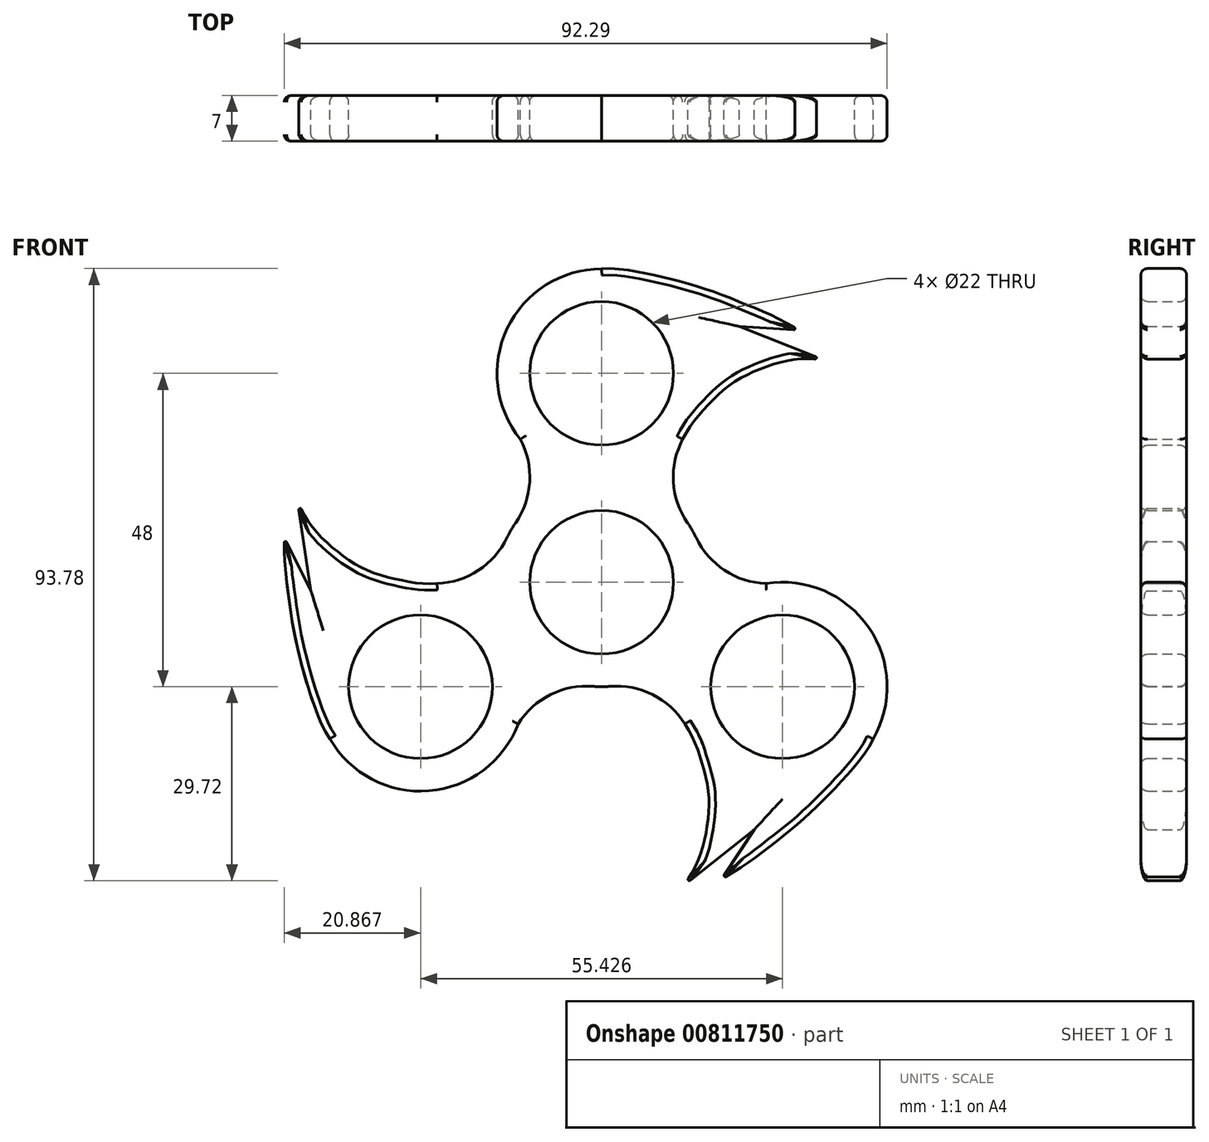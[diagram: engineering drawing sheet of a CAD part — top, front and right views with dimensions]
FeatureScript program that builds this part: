
annotation { "Feature Type Name" : "Feature", "Feature Type Description" : "" }
export const myFeature = defineFeature(function(context is Context, id is Id, definition is map)
    precondition{}
    {
        {
            var Q0;
            Q0=qCreatedBy(makeId("Front.planeOp"),FACE);
            var sketch = newSketch(context, id + "F0", { "sketchPlane" : qUnion([Q0])});
            skCircle(sketch, "E0", {"center": v(0, 0) * mm, "radius": 11 * mm});
            skArc(sketch, "E1", {"start": v(-13.17, 9.09) * mm, "mid": v(0, -16) * mm, "end": v(13.17, 9.09) * mm});
            skCircle(sketch, "E2", {"center": v(0, 32) * mm, "radius": 11 * mm});
            skLineSegment(sketch, "E3", {"start": v(12.42, 21.9) * mm, "end": v(12.42, 21.9) * mm});
            skFitSpline(sketch, "E4", {"points": [v(0, 48) * mm, v(15.63, 45) * mm, v(22.11, 42.54) * mm, v(30.28, 38.63) * mm], "startDerivative": vector(23.83, 2.95) * mm, "endDerivative": vector(45.32, -25.65) * mm});
            skLineSegment(sketch, "E5", {"start": v(30.28, 38.63) * mm, "end": v(21.1, 39.2) * mm});
            skLineSegment(sketch, "E6", {"start": v(21.1, 39.2) * mm, "end": v(34.96, 33.72) * mm});
            skFitSpline(sketch, "E7", {"points": [v(34.96, 33.72) * mm, v(23.56, 32.37) * mm, v(18.65, 29.47) * mm, v(15.85, 26.67) * mm, v(12.42, 21.9) * mm], "startDerivative": vector(-35.39, 11.82) * mm, "endDerivative": vector(-17.96, -33.28) * mm});
            skArc(sketch, "E8.trimOffspring", {"start": v(0, 48) * mm, "mid": v(-14.45, 38.88) * mm, "end": v(-12.42, 21.9) * mm});
            skArc(sketch, "E9", {"start": v(13.17, 9.09) * mm, "mid": v(11, 15.4) * mm, "end": v(12.42, 21.9) * mm});
            skArc(sketch, "E10.MirrorCS", {"start": v(-13.17, 9.09) * mm, "mid": v(-11, 15.4) * mm, "end": v(-12.42, 21.9) * mm});
            skSolve(sketch);
        }
        {
            var Q0;
            Q0=makeQuery(id+"F0.imprint","IMPRINT",FACE,{"disambiguationData":[TD([[makeQuery(id+"F0.imprint","IMPRINT",EDGE,{"derivedFrom":sQuery(id+"F0.wireOp",EDGE,"E0")}),-1.0]])]});
            extrude(context, id + "F1", {"entities" : qUnion([Q0]), "depth" : 7 * mm, "offsetDistance" : 25 * mm});
        }
        {
            var Q0;
            Q0=makeQuery(id+"F1.opExtrude","SWEPT_BODY",BODY,{"disambiguationData":[OSD([sQuery(id+"F0.wireOp",EDGE,"E0"),sQuery(id+"F0.wireOp",EDGE,"E1"),sQuery(id+"F0.wireOp",EDGE,"E2"),sQuery(id+"F0.wireOp",EDGE,"E3"),sQuery(id+"F0.wireOp",EDGE,"LkXJ2vyM-1mGQ-eDcK-5ijq-w6ZpazgIBIUJ"),sQuery(id+"F0.wireOp",EDGE,"5baaefb0-8613-44b4-96e0-c200b75026c80.MirrorCS"),sQuery(id+"F0.wireOp",EDGE,"E4"),sQuery(id+"F0.wireOp",EDGE,"E5"),sQuery(id+"F0.wireOp",EDGE,"E6"),sQuery(id+"F0.wireOp",EDGE,"E7"),sQuery(id+"F0.wireOp",EDGE,"E8.trimOffspring")])]});
            var Q1;
            Q1=makeQuery(id+"F1.opExtrude","SWEPT_FACE",FACE,{"disambiguationData":[OSD([sQuery(id+"F0.wireOp",EDGE,"E1")])]});
            circularPattern(context, id + "F2", {"entities" : qUnion([Q0]), "axis" : qUnion([Q1]), "angle" : 360 * degree, "instanceCount" : 3, "equalSpace" : true});
        }
        {
            var Q0;
            Q0=makeQuery(id+"F1.opExtrude","SWEPT_BODY",BODY,{"disambiguationData":[OSD([sQuery(id+"F0.wireOp",EDGE,"E0"),sQuery(id+"F0.wireOp",EDGE,"E1"),sQuery(id+"F0.wireOp",EDGE,"E2"),sQuery(id+"F0.wireOp",EDGE,"E3"),sQuery(id+"F0.wireOp",EDGE,"LkXJ2vyM-1mGQ-eDcK-5ijq-w6ZpazgIBIUJ"),sQuery(id+"F0.wireOp",EDGE,"5baaefb0-8613-44b4-96e0-c200b75026c80.MirrorCS"),sQuery(id+"F0.wireOp",EDGE,"E4"),sQuery(id+"F0.wireOp",EDGE,"E5"),sQuery(id+"F0.wireOp",EDGE,"E6"),sQuery(id+"F0.wireOp",EDGE,"E7"),sQuery(id+"F0.wireOp",EDGE,"E8.trimOffspring")])]});
            var Q1;
            Q1=makeQuery(id+"F2.opPattern","COPY",BODY,{"derivedFrom":makeQuery(id+"F1.opExtrude","SWEPT_BODY",BODY,{"disambiguationData":[OSD([sQuery(id+"F0.wireOp",EDGE,"E0"),sQuery(id+"F0.wireOp",EDGE,"E1"),sQuery(id+"F0.wireOp",EDGE,"E2"),sQuery(id+"F0.wireOp",EDGE,"E3"),sQuery(id+"F0.wireOp",EDGE,"LkXJ2vyM-1mGQ-eDcK-5ijq-w6ZpazgIBIUJ"),sQuery(id+"F0.wireOp",EDGE,"5baaefb0-8613-44b4-96e0-c200b75026c80.MirrorCS"),sQuery(id+"F0.wireOp",EDGE,"E4"),sQuery(id+"F0.wireOp",EDGE,"E5"),sQuery(id+"F0.wireOp",EDGE,"E6"),sQuery(id+"F0.wireOp",EDGE,"E7"),sQuery(id+"F0.wireOp",EDGE,"E8.trimOffspring")])]}),"instanceName":"1"});
            var Q2;
            Q2=makeQuery(id+"F2.opPattern","COPY",BODY,{"derivedFrom":makeQuery(id+"F1.opExtrude","SWEPT_BODY",BODY,{"disambiguationData":[OSD([sQuery(id+"F0.wireOp",EDGE,"E0"),sQuery(id+"F0.wireOp",EDGE,"E1"),sQuery(id+"F0.wireOp",EDGE,"E2"),sQuery(id+"F0.wireOp",EDGE,"E3"),sQuery(id+"F0.wireOp",EDGE,"LkXJ2vyM-1mGQ-eDcK-5ijq-w6ZpazgIBIUJ"),sQuery(id+"F0.wireOp",EDGE,"5baaefb0-8613-44b4-96e0-c200b75026c80.MirrorCS"),sQuery(id+"F0.wireOp",EDGE,"E4"),sQuery(id+"F0.wireOp",EDGE,"E5"),sQuery(id+"F0.wireOp",EDGE,"E6"),sQuery(id+"F0.wireOp",EDGE,"E7"),sQuery(id+"F0.wireOp",EDGE,"E8.trimOffspring")])]}),"instanceName":"2"});
            booleanBodies(context, id + "F3", {"operationType" : BooleanOperationType.UNION, "tools" : qUnion([Q0, Q1, Q2])});
        }
        {
            var Q0;
            {var subQ0=makeQuery(id+"F1.opExtrude","CAP_FACE",FACE,{"disambiguationData":[OSD([sQuery(id+"F0.wireOp",EDGE,"E0"),sQuery(id+"F0.wireOp",EDGE,"E1"),sQuery(id+"F0.wireOp",EDGE,"E2"),sQuery(id+"F0.wireOp",EDGE,"LkXJ2vyM-1mGQ-eDcK-5ijq-w6ZpazgIBIUJ"),sQuery(id+"F0.wireOp",EDGE,"5baaefb0-8613-44b4-96e0-c200b75026c80.MirrorCS"),sQuery(id+"F0.wireOp",EDGE,"E4"),sQuery(id+"F0.wireOp",EDGE,"E5"),sQuery(id+"F0.wireOp",EDGE,"E6"),sQuery(id+"F0.wireOp",EDGE,"E7"),sQuery(id+"F0.wireOp",EDGE,"E8.trimOffspring")])],"isStart":false});Q0=makeQuery(id+"F3.opBoolean","MERGE",FACE,{"derivedFrom":[subQ0,makeQuery(id+"F2.opPattern","COPY",FACE,{"derivedFrom":subQ0,"instanceName":"1"}),makeQuery(id+"F2.opPattern","COPY",FACE,{"derivedFrom":subQ0,"instanceName":"2"})]});}
            var Q1;
            {var subQ0=makeQuery(id+"F1.opExtrude","CAP_FACE",FACE,{"disambiguationData":[OSD([sQuery(id+"F0.wireOp",EDGE,"E0"),sQuery(id+"F0.wireOp",EDGE,"E1"),sQuery(id+"F0.wireOp",EDGE,"E2"),sQuery(id+"F0.wireOp",EDGE,"LkXJ2vyM-1mGQ-eDcK-5ijq-w6ZpazgIBIUJ"),sQuery(id+"F0.wireOp",EDGE,"5baaefb0-8613-44b4-96e0-c200b75026c80.MirrorCS"),sQuery(id+"F0.wireOp",EDGE,"E4"),sQuery(id+"F0.wireOp",EDGE,"E5"),sQuery(id+"F0.wireOp",EDGE,"E6"),sQuery(id+"F0.wireOp",EDGE,"E7"),sQuery(id+"F0.wireOp",EDGE,"E8.trimOffspring")])],"isStart":true});Q1=makeQuery(id+"F3.opBoolean","MERGE",FACE,{"derivedFrom":[subQ0,makeQuery(id+"F2.opPattern","COPY",FACE,{"derivedFrom":subQ0,"instanceName":"1"}),makeQuery(id+"F2.opPattern","COPY",FACE,{"derivedFrom":subQ0,"instanceName":"2"})]});}
            fillet(context, id + "F4", {"entities" : qUnion([Q0, Q1]), "radius" : 1 * mm, "tangentPropagation" : true, "allowEdgeOverflow" : false});
        }
        {
            var Q0;
            Q0=makeQuery(id+"F2.opPattern","COPY",EDGE,{"derivedFrom":makeQuery(id+"F1.opExtrude","SWEPT_EDGE",EDGE,{"disambiguationData":[OSD([sQuery(id+"F0.wireOp",EDGE,"E4"),sQuery(id+"F0.wireOp",EDGE,"E5")])]}),"instanceName":"2"});
            var Q1;
            Q1=makeQuery(id+"F2.opPattern","COPY",EDGE,{"derivedFrom":makeQuery(id+"F1.opExtrude","SWEPT_EDGE",EDGE,{"disambiguationData":[OSD([sQuery(id+"F0.wireOp",EDGE,"E6"),sQuery(id+"F0.wireOp",EDGE,"E7")])]}),"instanceName":"2"});
            var Q2;
            Q2=makeQuery(id+"F1.opExtrude","SWEPT_EDGE",EDGE,{"disambiguationData":[OSD([sQuery(id+"F0.wireOp",EDGE,"E6"),sQuery(id+"F0.wireOp",EDGE,"E7")])]});
            var Q3;
            Q3=makeQuery(id+"F1.opExtrude","SWEPT_EDGE",EDGE,{"disambiguationData":[OSD([sQuery(id+"F0.wireOp",EDGE,"E4"),sQuery(id+"F0.wireOp",EDGE,"E5")])]});
            var Q4;
            Q4=makeQuery(id+"F2.opPattern","COPY",EDGE,{"derivedFrom":makeQuery(id+"F1.opExtrude","SWEPT_EDGE",EDGE,{"disambiguationData":[OSD([sQuery(id+"F0.wireOp",EDGE,"E4"),sQuery(id+"F0.wireOp",EDGE,"E5")])]}),"instanceName":"1"});
            var Q5;
            Q5=makeQuery(id+"F2.opPattern","COPY",EDGE,{"derivedFrom":makeQuery(id+"F1.opExtrude","SWEPT_EDGE",EDGE,{"disambiguationData":[OSD([sQuery(id+"F0.wireOp",EDGE,"E6"),sQuery(id+"F0.wireOp",EDGE,"E7")])]}),"instanceName":"1"});
            fillet(context, id + "F5", {"entities" : qUnion([Q0, Q1, Q2, Q3, Q4, Q5]), "radius" : 0.2 * mm, "tangentPropagation" : true, "allowEdgeOverflow" : false});
        }
    });
